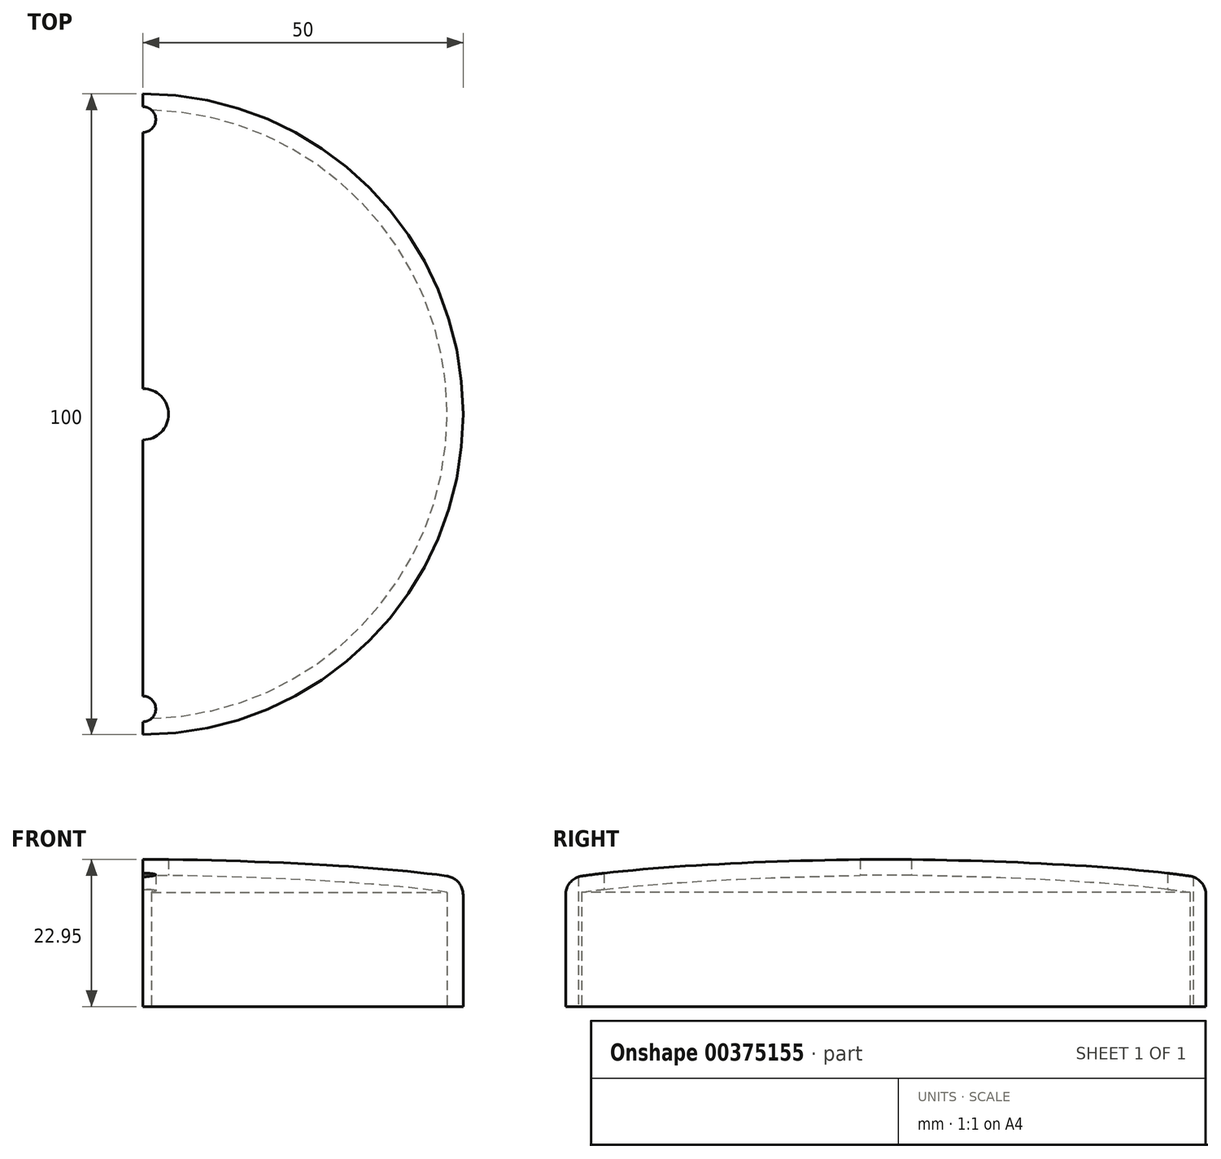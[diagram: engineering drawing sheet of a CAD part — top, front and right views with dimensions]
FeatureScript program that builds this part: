
annotation { "Feature Type Name" : "Feature", "Feature Type Description" : "" }
export const myFeature = defineFeature(function(context is Context, id is Id, definition is map)
    precondition{}
    {
        {
            var Q0;
            Q0=qCreatedBy(makeId("Top.planeOp"),FACE);
            var sketch = newSketch(context, id + "F0", { "sketchPlane" : qUnion([Q0])});
            skLineSegment(sketch, "E0", {"start": v(0, 90.49) * mm, "end": v(0, -102.2) * mm, "construction": true});
            skLineSegment(sketch, "E1", {"start": v(0, 50) * mm, "end": v(0, -50) * mm});
            skArc(sketch, "E2", {"start": v(0, 50) * mm, "mid": v(50, 0) * mm, "end": v(0, -50) * mm});
            skArc(sketch, "E3.MirrorCS", {"start": v(0, 50) * mm, "mid": v(-50, 0) * mm, "end": v(0, -50) * mm});
            skSolve(sketch);
        }
        {
            var Q0;
            Q0=makeQuery(id+"F0.imprint","IMPRINT",FACE,{"disambiguationData":[TD([[makeQuery(id+"F0.imprint","IMPRINT",EDGE,{"derivedFrom":sQuery(id+"F0.wireOp",EDGE,"E1")}),-1.0]])]});
            var Q1;
            Q1=makeQuery(id+"F0.imprint","IMPRINT",FACE,{"disambiguationData":[TD([[makeQuery(id+"F0.imprint","IMPRINT",EDGE,{"derivedFrom":sQuery(id+"F0.wireOp",EDGE,"E1")}),1.0]])]});
            extrude(context, id + "F1", {"entities" : qUnion([Q0, Q1]), "depth" : 20 * mm});
        }
        {
            var Q0;
            Q0=qCreatedBy(makeId("Front.planeOp"),FACE);
            var sketch = newSketch(context, id + "F2", { "sketchPlane" : qUnion([Q0])});
            skLineSegment(sketch, "E4", {"start": v(0, 43.91) * mm, "end": v(0, -14.27) * mm, "construction": true});
            skLineSegment(sketch, "E5", {"start": v(0, 20) * mm, "end": v(0, 23) * mm});
            skFitSpline(sketch, "E6", {"points": [v(0, 23) * mm, v(50, 20) * mm], "startDerivative": vector(53.74, -0.45) * mm, "endDerivative": vector(35.8, -5.75) * mm});
            skLineSegment(sketch, "E7", {"start": v(0, 20) * mm, "end": v(50, 20) * mm});
            skLineSegment(sketch, "E8.left", {"start": v(0, 23) * mm, "end": v(0, 0) * mm});
            skSolve(sketch);
        }
        {
            var Q0;
            {var subQ0=sQuery(id+"F2.wireOp",EDGE,"E7");var subQ1=sQuery(id+"F2.wireOp",EDGE,"E6");var subQ2=makeQuery(id+"F2.imprint","INTERSECT",VERTEX,{"derivedFrom":[subQ1,subQ0]});Q0=makeQuery(id+"F2.imprint","IMPRINT",FACE,{"disambiguationData":[TD([[makeQuery(id+"F2.imprint","IMPRINT",EDGE,{"disambiguationData":[TD([[subQ2,1.0]])],"derivedFrom":subQ1}),-1.0]])]});}
            var Q1;
            {var subQ0=sQuery(id+"F2.wireOp",EDGE,"E8.left");var subQ5=sQuery(id+"F2.wireOp",EDGE,"E7");var subQ6=makeQuery(id+"F2.imprint","INTERSECT",VERTEX,{"derivedFrom":[subQ5,subQ0]});Q1=makeQuery(id+"F2.imprint","IMPRINT",FACE,{"disambiguationData":[TD([[makeQuery(id+"F2.imprint","IMPRINT",EDGE,{"disambiguationData":[TD([[subQ6,-1.0]])],"derivedFrom":subQ5}),1.0]])]});}
            var Q2;
            Q2=sQuery(id+"F2.wireOp",EDGE,"E5");
            revolve(context, id + "F3", {"operationType" : NewBodyOperationType.ADD, "entities" : qUnion([Q0, Q1]), "axis" : qUnion([Q2]), "revolveType" : RevolveType.FULL});
        }
        {
            var Q0;
            Q0=qCreatedBy(makeId("Front.planeOp"),FACE);
            var sketch = newSketch(context, id + "F4", { "sketchPlane" : qUnion([Q0])});
            skLineSegment(sketch, "E9.bottom", {"start": v(0, 52.26) * mm, "end": v(-69.78, 52.26) * mm});
            skLineSegment(sketch, "E9.top", {"start": v(0, -40.02) * mm, "end": v(-69.78, -40.02) * mm});
            skLineSegment(sketch, "E9.left", {"start": v(0, 52.26) * mm, "end": v(0, -40.02) * mm});
            skLineSegment(sketch, "E9.right", {"start": v(-69.78, 52.26) * mm, "end": v(-69.78, -40.02) * mm});
            skSolve(sketch);
        }
        {
            var Q0;
            Q0 = qSketchRegion(id + "F4", true);
            extrude(context, id + "F5", {"entities" : qUnion([Q0]), "operationType" : NewBodyOperationType.REMOVE, "endBound" : BoundingType.SYMMETRIC, "oppositeDirection" : true, "depth" : 100 * mm});
        }
        {
            var Q0;
            Q0=makeQuery(id+"F5.boolean.opBoolean","COPY",FACE,{"derivedFrom":makeQuery(id+"F5.opExtrude","SWEPT_FACE",FACE,{"disambiguationData":[OSD([sQuery(id+"F4.wireOp",EDGE,"E9.left")])]})});
            shell(context, id + "F6", {"entities" : qUnion([Q0]), "thickness" : 2.5 * mm});
        }
        {
            var Q0;
            {var subQ0=sQuery(id+"F0.wireOp",EDGE,"E3.MirrorCS");var subQ1=sQuery(id+"F0.wireOp",EDGE,"E2");Q0=makeQuery(id+"F6.opShell","OFFSET_FACE",FACE,{"disambiguationData":[OSD([subQ1,subQ0]),TDD([makeQuery(id+"F1.opExtrude","CAP_FACE",FACE,{"disambiguationData":[OSD([subQ1,subQ0])],"isStart":true})])]});}
            extrude(context, id + "F7", {"entities" : qUnion([Q0]), "operationType" : NewBodyOperationType.REMOVE, "oppositeDirection" : true, "depth" : 2.5 * mm});
        }
        {
            var Q0;
            Q0=qCreatedBy(makeId("Top.planeOp"),FACE);
            var sketch = newSketch(context, id + "F8", { "sketchPlane" : qUnion([Q0])});
            skCircle(sketch, "E10", {"center": v(0, 46) * mm, "radius": 2 * mm});
            skCircle(sketch, "E11.MirrorC", {"center": v(0, -46) * mm, "radius": 2 * mm});
            skSolve(sketch);
        }
        {
            var Q0;
            Q0 = qSketchRegion(id + "F8", true);
            extrude(context, id + "F9", {"entities" : qUnion([Q0]), "operationType" : NewBodyOperationType.REMOVE, "depth" : 25 * mm});
        }
        {
            var Q0;
            Q0=qCreatedBy(makeId("Top.planeOp"),FACE);
            var sketch = newSketch(context, id + "F10", { "sketchPlane" : qUnion([Q0])});
            skCircle(sketch, "E12", {"center": v(0, 0) * mm, "radius": 4 * mm});
            skSolve(sketch);
        }
        {
            var Q0;
            Q0 = qSketchRegion(id + "F10", true);
            extrude(context, id + "F11", {"entities" : qUnion([Q0]), "operationType" : NewBodyOperationType.REMOVE, "depth" : 25 * mm});
        }
        {
            var Q0;
            Q0=makeQuery(id+"F3.boolean.opBoolean","MERGE",EDGE,{"derivedFrom":[makeQuery(id+"F1.opExtrude","CAP_EDGE",EDGE,{"disambiguationData":[OSD([sQuery(id+"F0.wireOp",EDGE,"E2"),sQuery(id+"F0.wireOp",EDGE,"E3.MirrorCS")])],"isStart":false}),makeQuery(id+"F3.opRevolve","SWEPT_EDGE",EDGE,{"disambiguationData":[OSD([sQuery(id+"F2.wireOp",EDGE,"E6"),sQuery(id+"F2.wireOp",EDGE,"E7")])]})]});
            fillet(context, id + "F12", {"entities" : qUnion([Q0]), "radius" : 3 * mm, "tangentPropagation" : true, "allowEdgeOverflow" : false});
        }
    });
